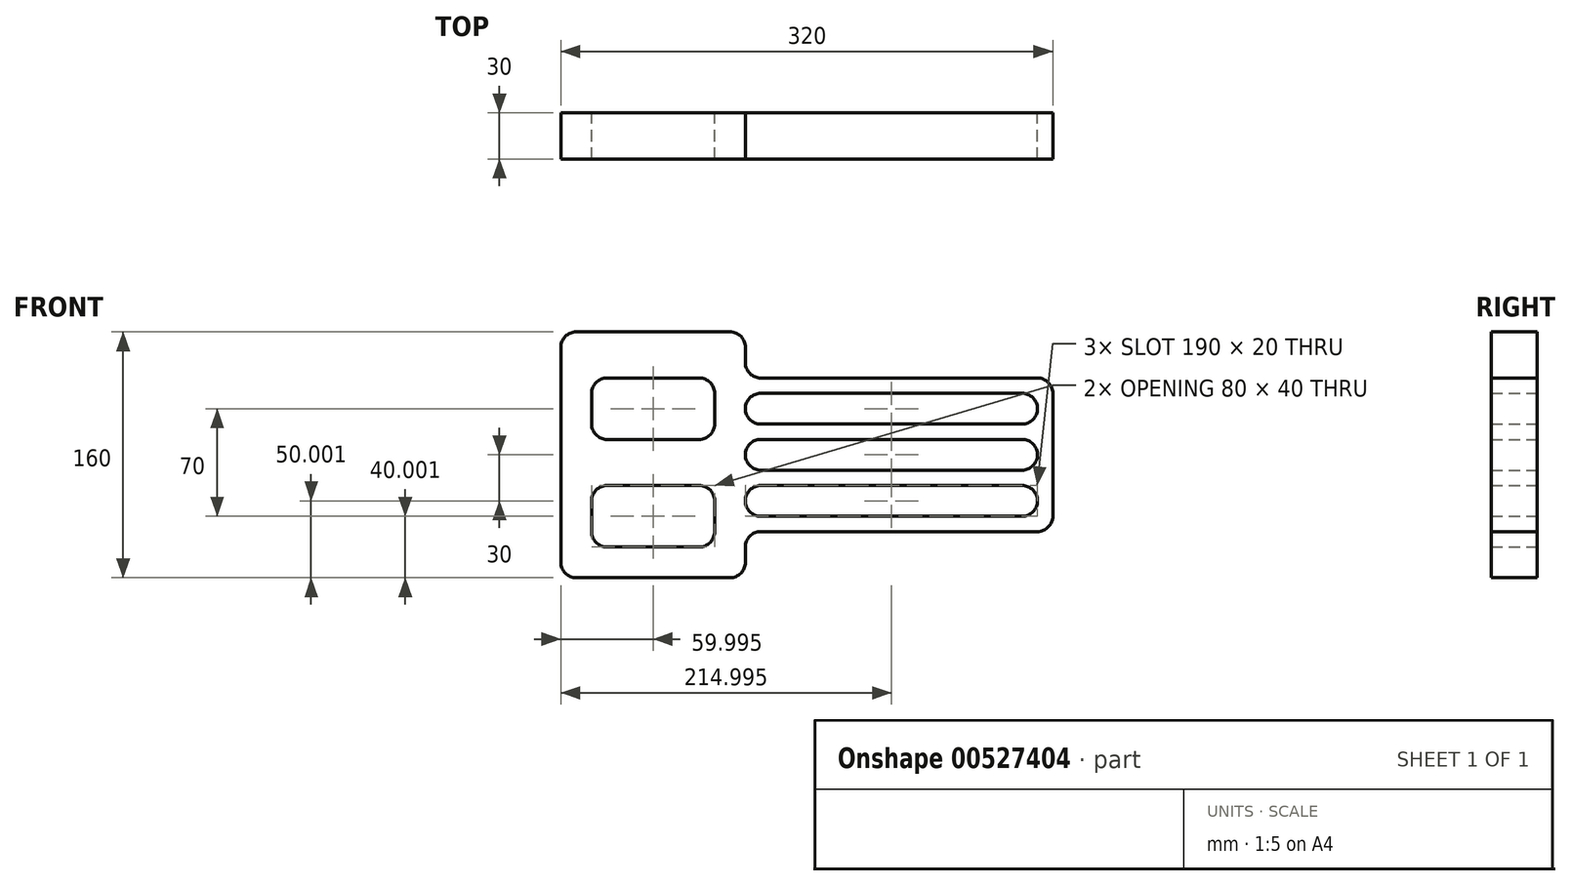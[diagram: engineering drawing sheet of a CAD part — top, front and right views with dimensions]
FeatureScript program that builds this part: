
annotation { "Feature Type Name" : "Feature", "Feature Type Description" : "" }
export const myFeature = defineFeature(function(context is Context, id is Id, definition is map)
    precondition{}
    {
        {
            var Q0;
            Q0=qCreatedBy(makeId("Front.planeOp"),FACE);
            var sketch = newSketch(context, id + "F0", { "sketchPlane" : qUnion([Q0])});
            skLineSegment(sketch, "E0", {"start": v(-132.3, 93.52) * mm, "end": v(-32.3, 93.52) * mm});
            skLineSegment(sketch, "E1", {"start": v(-22.3, 83.52) * mm, "end": v(-22.3, 73.52) * mm});
            skLineSegment(sketch, "E2", {"start": v(-12.3, 63.52) * mm, "end": v(167.7, 63.52) * mm});
            skLineSegment(sketch, "E3", {"start": v(177.7, 53.52) * mm, "end": v(177.7, -26.48) * mm});
            skLineSegment(sketch, "E4", {"start": v(167.7, -36.48) * mm, "end": v(-12.3, -36.48) * mm});
            skLineSegment(sketch, "E5", {"start": v(-22.3, -46.48) * mm, "end": v(-22.3, -56.48) * mm});
            skLineSegment(sketch, "E6", {"start": v(-32.3, -66.48) * mm, "end": v(-132.3, -66.48) * mm});
            skLineSegment(sketch, "E7", {"start": v(-142.3, -56.48) * mm, "end": v(-142.3, 83.52) * mm});
            skLineSegment(sketch, "E8", {"start": v(-112.3, 63.52) * mm, "end": v(-52.3, 63.52) * mm});
            skLineSegment(sketch, "E9", {"start": v(-42.3, 53.52) * mm, "end": v(-42.3, 33.52) * mm});
            skLineSegment(sketch, "E10", {"start": v(-52.3, 23.52) * mm, "end": v(-112.3, 23.52) * mm});
            skLineSegment(sketch, "E11", {"start": v(-122.3, 33.52) * mm, "end": v(-122.3, 53.52) * mm});
            skLineSegment(sketch, "E12.bottom", {"start": v(-112.3, -6.48) * mm, "end": v(-52.3, -6.48) * mm});
            skLineSegment(sketch, "E12.top", {"start": v(-112.3, -46.48) * mm, "end": v(-52.3, -46.48) * mm});
            skLineSegment(sketch, "E12.left", {"start": v(-122.3, -16.48) * mm, "end": v(-122.3, -36.48) * mm});
            skLineSegment(sketch, "E12.right", {"start": v(-42.3, -16.48) * mm, "end": v(-42.3, -36.48) * mm});
            skPoint(sketch, "E13.visualSharp", {"position": v(-22.3, -36.48) * mm});
            skArc(sketch, "E13.filletArc", {"start": v(-12.3, -36.48) * mm, "mid": v(-19.38, -39.4) * mm, "end": v(-22.3, -46.48) * mm});
            skPoint(sketch, "E14.visualSharp", {"position": v(-22.3, 63.52) * mm});
            skArc(sketch, "E14.filletArc", {"start": v(-22.3, 73.52) * mm, "mid": v(-19.38, 66.45) * mm, "end": v(-12.3, 63.52) * mm});
            skPoint(sketch, "E15.visualSharp", {"position": v(-142.3, 93.52) * mm});
            skArc(sketch, "E15.filletArc", {"start": v(-132.3, 93.52) * mm, "mid": v(-139.38, 90.6) * mm, "end": v(-142.3, 83.52) * mm});
            skPoint(sketch, "E16.visualSharp", {"position": v(-142.3, -66.48) * mm});
            skArc(sketch, "E16.filletArc", {"start": v(-142.3, -56.48) * mm, "mid": v(-139.38, -63.55) * mm, "end": v(-132.3, -66.48) * mm});
            skPoint(sketch, "E17.visualSharp", {"position": v(177.7, -36.48) * mm});
            skArc(sketch, "E17.filletArc", {"start": v(167.7, -36.48) * mm, "mid": v(174.77, -33.55) * mm, "end": v(177.7, -26.48) * mm});
            skPoint(sketch, "E18.visualSharp", {"position": v(177.7, 63.52) * mm});
            skArc(sketch, "E18.filletArc", {"start": v(177.7, 53.52) * mm, "mid": v(174.77, 60.6) * mm, "end": v(167.7, 63.52) * mm});
            skPoint(sketch, "E19.visualSharp", {"position": v(-122.3, 23.52) * mm});
            skArc(sketch, "E19.filletArc", {"start": v(-122.3, 33.52) * mm, "mid": v(-119.38, 26.45) * mm, "end": v(-112.3, 23.52) * mm});
            skPoint(sketch, "E20.visualSharp", {"position": v(-122.3, 63.52) * mm});
            skArc(sketch, "E20.filletArc", {"start": v(-112.3, 63.52) * mm, "mid": v(-119.38, 60.6) * mm, "end": v(-122.3, 53.52) * mm});
            skPoint(sketch, "E21.visualSharp", {"position": v(-42.3, 63.52) * mm});
            skArc(sketch, "E21.filletArc", {"start": v(-42.3, 53.52) * mm, "mid": v(-45.23, 60.6) * mm, "end": v(-52.3, 63.52) * mm});
            skPoint(sketch, "E22.visualSharp", {"position": v(-42.3, 23.52) * mm});
            skArc(sketch, "E22.filletArc", {"start": v(-52.3, 23.52) * mm, "mid": v(-45.23, 26.45) * mm, "end": v(-42.3, 33.52) * mm});
            skPoint(sketch, "E23.visualSharp", {"position": v(-42.3, -6.48) * mm});
            skArc(sketch, "E23.filletArc", {"start": v(-42.3, -16.48) * mm, "mid": v(-45.23, -9.4) * mm, "end": v(-52.3, -6.48) * mm});
            skPoint(sketch, "E24.visualSharp", {"position": v(-122.3, -6.48) * mm});
            skArc(sketch, "E24.filletArc", {"start": v(-112.3, -6.48) * mm, "mid": v(-119.38, -9.4) * mm, "end": v(-122.3, -16.48) * mm});
            skPoint(sketch, "E25.visualSharp", {"position": v(-122.3, -46.48) * mm});
            skArc(sketch, "E25.filletArc", {"start": v(-122.3, -36.48) * mm, "mid": v(-119.38, -43.55) * mm, "end": v(-112.3, -46.48) * mm});
            skPoint(sketch, "E26.visualSharp", {"position": v(-42.3, -46.48) * mm});
            skArc(sketch, "E26.filletArc", {"start": v(-52.3, -46.48) * mm, "mid": v(-45.23, -43.55) * mm, "end": v(-42.3, -36.48) * mm});
            skLineSegment(sketch, "E27.bottom", {"start": v(-12.3, 53.52) * mm, "end": v(157.7, 53.52) * mm});
            skLineSegment(sketch, "E27.top", {"start": v(-12.3, 33.52) * mm, "end": v(157.7, 33.52) * mm});
            skLineSegment(sketch, "E27.left", {"start": v(-22.3, 43.52) * mm, "end": v(-22.3, 43.52) * mm});
            skLineSegment(sketch, "E27.right", {"start": v(167.7, 43.52) * mm, "end": v(167.7, 43.52) * mm});
            skLineSegment(sketch, "E28.bottom", {"start": v(-12.3, 23.52) * mm, "end": v(157.7, 23.52) * mm});
            skLineSegment(sketch, "E28.top", {"start": v(-12.3, 3.52) * mm, "end": v(157.7, 3.52) * mm});
            skLineSegment(sketch, "E28.left", {"start": v(-22.3, 13.52) * mm, "end": v(-22.3, 13.52) * mm});
            skLineSegment(sketch, "E28.right", {"start": v(167.7, 13.52) * mm, "end": v(167.7, 13.52) * mm});
            skLineSegment(sketch, "E29.bottom", {"start": v(-12.3, -6.48) * mm, "end": v(157.7, -6.48) * mm});
            skLineSegment(sketch, "E29.top", {"start": v(-12.3, -26.48) * mm, "end": v(157.7, -26.48) * mm});
            skLineSegment(sketch, "E29.left", {"start": v(-22.3, -16.48) * mm, "end": v(-22.3, -16.48) * mm});
            skLineSegment(sketch, "E29.right", {"start": v(167.7, -16.48) * mm, "end": v(167.7, -16.48) * mm});
            skPoint(sketch, "E30.visualSharp", {"position": v(-22.3, 53.52) * mm});
            skArc(sketch, "E30.filletArc", {"start": v(-12.3, 53.52) * mm, "mid": v(-19.38, 50.6) * mm, "end": v(-22.3, 43.52) * mm});
            skPoint(sketch, "E31.visualSharp", {"position": v(-22.3, 33.52) * mm});
            skArc(sketch, "E31.filletArc", {"start": v(-22.3, 43.52) * mm, "mid": v(-19.38, 36.45) * mm, "end": v(-12.3, 33.52) * mm});
            skArc(sketch, "E32.filletArc", {"start": v(167.7, 43.52) * mm, "mid": v(164.77, 50.6) * mm, "end": v(157.7, 53.52) * mm});
            skPoint(sketch, "E33.visualSharp", {"position": v(167.7, 33.52) * mm});
            skArc(sketch, "E33.filletArc", {"start": v(157.7, 33.52) * mm, "mid": v(164.77, 36.45) * mm, "end": v(167.7, 43.52) * mm});
            skPoint(sketch, "E34.visualSharp", {"position": v(167.7, 23.52) * mm});
            skArc(sketch, "E34.filletArc", {"start": v(167.7, 13.52) * mm, "mid": v(164.77, 20.6) * mm, "end": v(157.7, 23.52) * mm});
            skPoint(sketch, "E35.visualSharp", {"position": v(167.7, 3.52) * mm});
            skArc(sketch, "E35.filletArc", {"start": v(157.7, 3.52) * mm, "mid": v(164.77, 6.45) * mm, "end": v(167.7, 13.52) * mm});
            skPoint(sketch, "E36.visualSharp", {"position": v(-22.3, 23.52) * mm});
            skArc(sketch, "E36.filletArc", {"start": v(-12.3, 23.52) * mm, "mid": v(-19.38, 20.6) * mm, "end": v(-22.3, 13.52) * mm});
            skPoint(sketch, "E37.visualSharp", {"position": v(-22.3, 3.52) * mm});
            skArc(sketch, "E37.filletArc", {"start": v(-22.3, 13.52) * mm, "mid": v(-19.38, 6.45) * mm, "end": v(-12.3, 3.52) * mm});
            skPoint(sketch, "E38.visualSharp", {"position": v(-22.3, -6.48) * mm});
            skArc(sketch, "E38.filletArc", {"start": v(-12.3, -6.48) * mm, "mid": v(-19.38, -9.4) * mm, "end": v(-22.3, -16.48) * mm});
            skPoint(sketch, "E39.visualSharp", {"position": v(-22.3, -26.48) * mm});
            skArc(sketch, "E39.filletArc", {"start": v(-22.3, -16.48) * mm, "mid": v(-19.38, -23.55) * mm, "end": v(-12.3, -26.48) * mm});
            skPoint(sketch, "E40.visualSharp", {"position": v(167.7, -6.48) * mm});
            skArc(sketch, "E40.filletArc", {"start": v(167.7, -16.48) * mm, "mid": v(164.77, -9.4) * mm, "end": v(157.7, -6.48) * mm});
            skArc(sketch, "E41.filletArc", {"start": v(157.7, -26.48) * mm, "mid": v(164.77, -23.55) * mm, "end": v(167.7, -16.48) * mm});
            skPoint(sketch, "E42.visualSharp", {"position": v(-22.3, 93.52) * mm});
            skArc(sketch, "E42.filletArc", {"start": v(-22.3, 83.52) * mm, "mid": v(-25.23, 90.6) * mm, "end": v(-32.3, 93.52) * mm});
            skPoint(sketch, "E43.visualSharp", {"position": v(-22.3, -66.48) * mm});
            skArc(sketch, "E43.filletArc", {"start": v(-32.3, -66.48) * mm, "mid": v(-25.23, -63.55) * mm, "end": v(-22.3, -56.48) * mm});
            skSolve(sketch);
        }
        {
            var Q0;
            Q0=makeQuery(id+"F0.imprint","IMPRINT",FACE,{"disambiguationData":[TD([[makeQuery(id+"F0.imprint","IMPRINT",EDGE,{"derivedFrom":sQuery(id+"F0.wireOp",EDGE,"E0")}),-1.0]])]});
            extrude(context, id + "F1", {"entities" : qUnion([Q0]), "depth" : 30 * mm, "offsetDistance" : 25 * mm});
        }
    });
